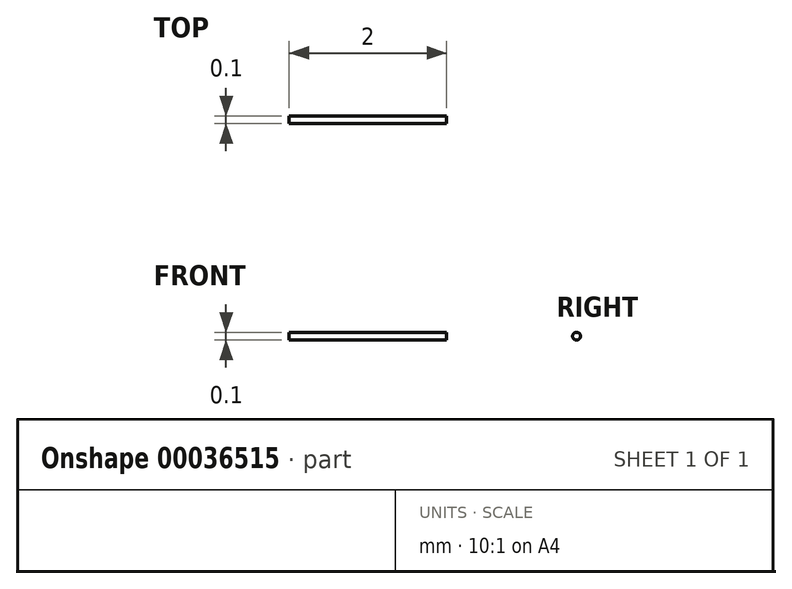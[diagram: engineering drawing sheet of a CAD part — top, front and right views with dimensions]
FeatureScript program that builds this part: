
annotation { "Feature Type Name" : "Feature", "Feature Type Description" : "" }
export const myFeature = defineFeature(function(context is Context, id is Id, definition is map)
    precondition{}
    {
        {
            var Q0;
            Q0=qCreatedBy(makeId("Right.planeOp"),FACE);
            var sketch = newSketch(context, id + "F0", { "sketchPlane" : qUnion([Q0])});
            skCircle(sketch, "E0", {"center": v(0, 0) * mm, "radius": 0.05 * mm});
            skSolve(sketch);
        }
        {
            var Q0;
            Q0=qSketchRegion(id+"F0",true);
            extrude(context, id + "F1", {"entities" : qUnion([Q0]), "depth" : 2 * mm, "offsetDistance" : 25 * mm});
        }
    });
